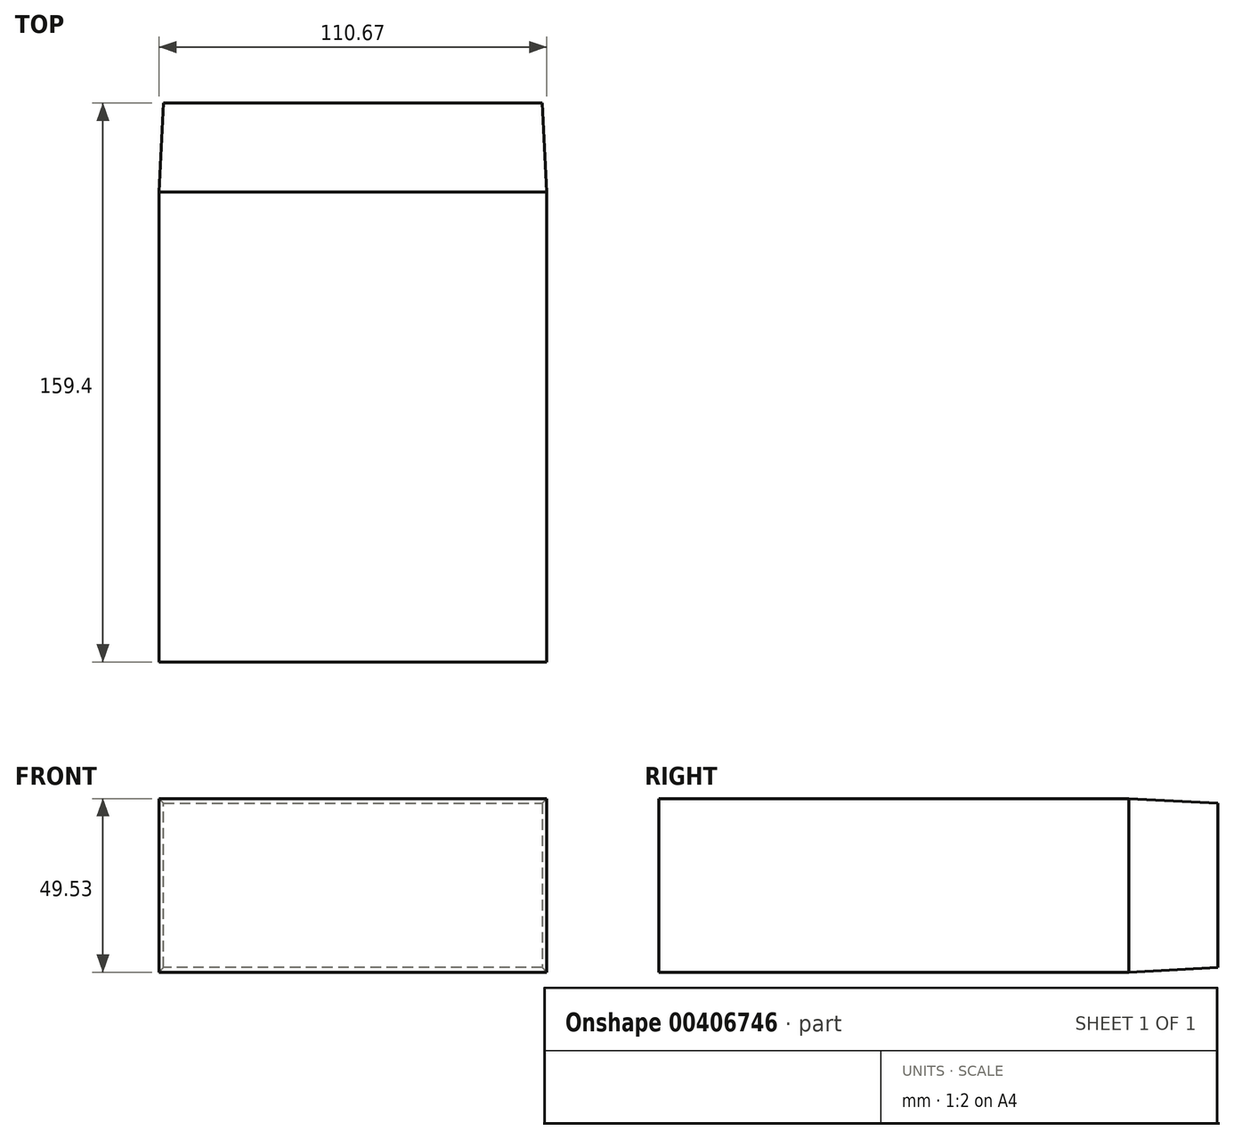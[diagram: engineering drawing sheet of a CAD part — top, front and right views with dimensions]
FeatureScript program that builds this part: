
annotation { "Feature Type Name" : "Feature", "Feature Type Description" : "" }
export const myFeature = defineFeature(function(context is Context, id is Id, definition is map)
    precondition{}
    {
        {
            var Q0;
            Q0=qCreatedBy(makeId("Front.planeOp"),FACE);
            var sketch = newSketch(context, id + "F0", { "sketchPlane" : qUnion([Q0])});
            skLineSegment(sketch, "E0.bottom", {"start": v(-57.3, 24.78) * mm, "end": v(50.7, 24.78) * mm});
            skLineSegment(sketch, "E0.top", {"start": v(-57.3, -22.09) * mm, "end": v(50.7, -22.09) * mm});
            skLineSegment(sketch, "E0.left", {"start": v(-57.3, 24.78) * mm, "end": v(-57.3, -22.09) * mm});
            skLineSegment(sketch, "E0.right", {"start": v(50.7, 24.78) * mm, "end": v(50.7, -22.09) * mm});
            skSolve(sketch);
        }
        {
            var Q0;
            Q0=makeQuery(id+"F0.imprint","IMPRINT",FACE,{"disambiguationData":[TD([[makeQuery(id+"F0.imprint","IMPRINT",EDGE,{"derivedFrom":sQuery(id+"F0.wireOp",EDGE,"E0.bottom")}),-1.0]])]});
            var sketch = newSketch(context, id + "F1", { "sketchPlane" : qUnion([Q0])});
            skSolve(sketch);
        }
        {
            var Q0;
            Q0=makeQuery(id+"F1.imprint","IMPRINT",FACE,{"disambiguationData":[TD([[makeQuery(id+"F1.imprint","IMPRINT",EDGE,{"derivedFrom":makeQuery(id+"F0.imprint","IMPRINT",EDGE,{"derivedFrom":sQuery(id+"F0.wireOp",EDGE,"E0.bottom")})}),-1.0]])]});
            extrude(context, id + "F2", {"entities" : qUnion([Q0]), "depth" : 25.4 * mm, "hasDraft" : true, "draftAngle" : 3 * degree});
        }
        {
            var Q0;
            Q0=makeQuery(id+"F2.opExtrude","CAP_FACE",FACE,{"disambiguationData":[OSD([sQuery(id+"F0.wireOp",EDGE,"E0.bottom"),sQuery(id+"F0.wireOp",EDGE,"E0.top"),sQuery(id+"F0.wireOp",EDGE,"E0.left"),sQuery(id+"F0.wireOp",EDGE,"E0.right")])],"isStart":false});
            extrude(context, id + "F3", {"entities" : qUnion([Q0]), "operationType" : NewBodyOperationType.ADD, "depth" : 134 * mm});
        }
    });
